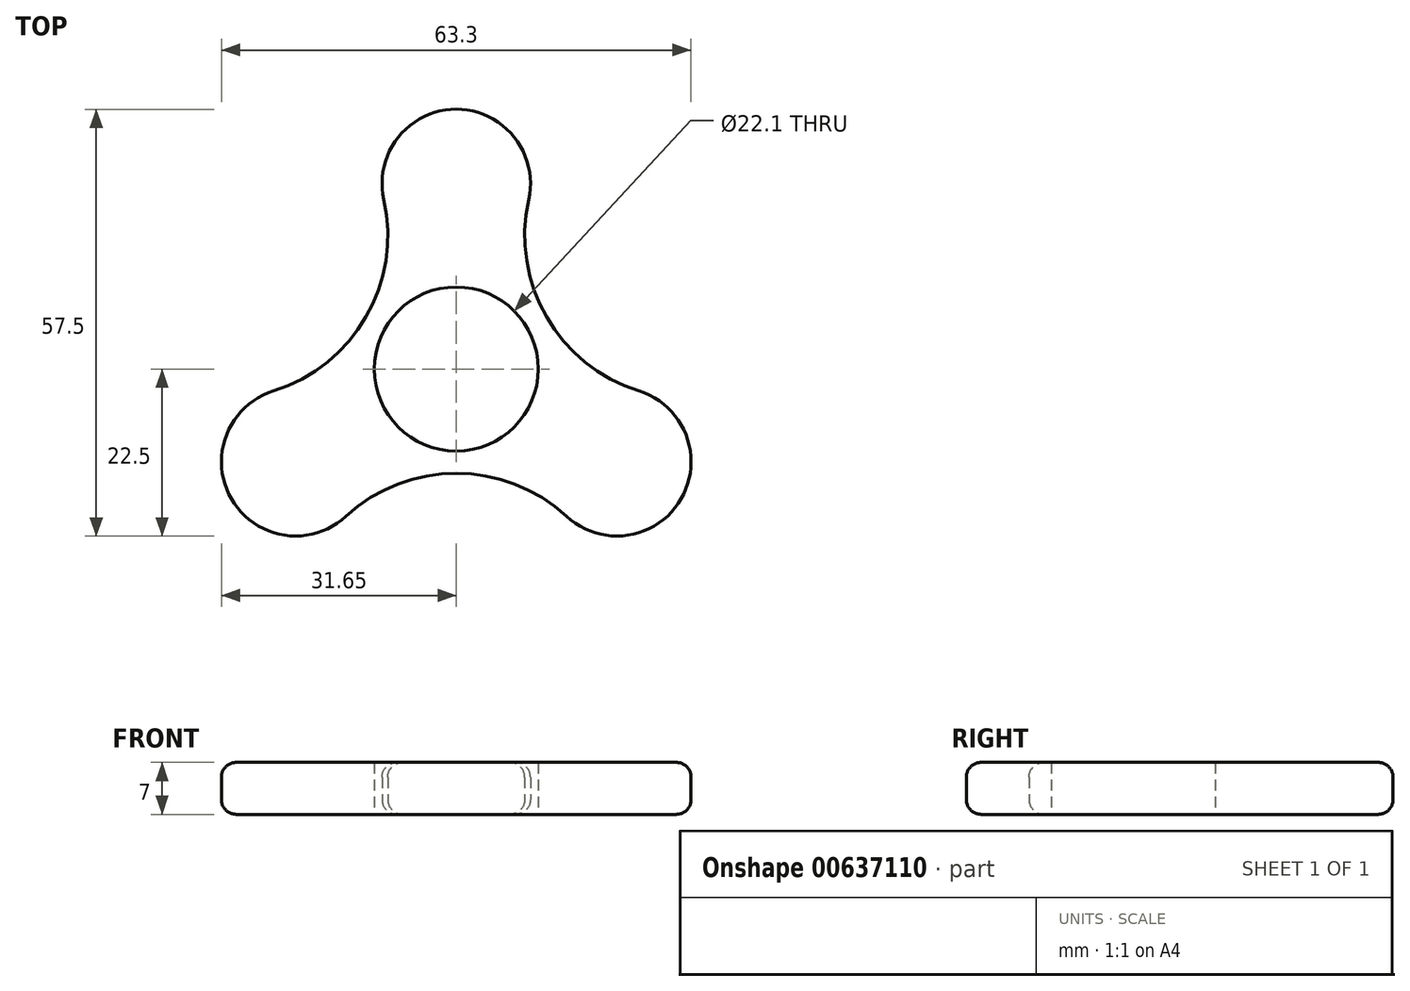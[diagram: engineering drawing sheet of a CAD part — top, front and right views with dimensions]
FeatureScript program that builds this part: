
annotation { "Feature Type Name" : "Feature", "Feature Type Description" : "" }
export const myFeature = defineFeature(function(context is Context, id is Id, definition is map)
    precondition{}
    {
        {
            var Q0;
            Q0=qCreatedBy(makeId("Top.planeOp"),FACE);
            var sketch = newSketch(context, id + "F0", { "sketchPlane" : qUnion([Q0])});
            skCircle(sketch, "E0", {"center": v(0, 0) * mm, "radius": 11.05 * mm});
            skLineSegment(sketch, "E1", {"start": v(0, 0) * mm, "end": v(0, 25) * mm});
            skLineSegment(sketch, "E2", {"start": v(0, 0) * mm, "end": v(-21.65, -12.5) * mm});
            skLineSegment(sketch, "E3", {"start": v(0, 0) * mm, "end": v(21.65, -12.5) * mm});
            skCircle(sketch, "E4", {"center": v(-21.65, -12.5) * mm, "radius": 10 * mm});
            skCircle(sketch, "E5", {"center": v(0, 25) * mm, "radius": 10 * mm});
            skCircle(sketch, "E6", {"center": v(21.65, -12.5) * mm, "radius": 10 * mm});
            skArc(sketch, "E7", {"start": v(-24.63, -2.96) * mm, "mid": v(-12.17, 7.03) * mm, "end": v(-9.76, 22.81) * mm});
            skArc(sketch, "E8", {"start": v(9.76, 22.81) * mm, "mid": v(12.17, 7.02) * mm, "end": v(24.63, -2.96) * mm});
            skArc(sketch, "E9", {"start": v(14.88, -19.86) * mm, "mid": v(0, -14.05) * mm, "end": v(-14.88, -19.86) * mm});
            skSolve(sketch);
        }
        {
            var Q0;
            {var subQ0=sQuery(id+"F0.wireOp",EDGE,"E4");var subQ1=makeQuery(id+"F0.imprint","INTERSECT",VERTEX,{"derivedFrom":[subQ0,sQuery(id+"F0.wireOp",EDGE,"E7")]});Q0=makeQuery(id+"F0.imprint","IMPRINT",FACE,{"disambiguationData":[TD([[makeQuery(id+"F0.imprint","IMPRINT",EDGE,{"disambiguationData":[TD([[subQ1,1.0]])],"derivedFrom":subQ0}),1.0]])]});}
            var Q1;
            {var subQ5=sQuery(id+"F0.wireOp",EDGE,"E7");Q1=makeQuery(id+"F0.imprint","IMPRINT",FACE,{"disambiguationData":[TD([[makeQuery(id+"F0.imprint","IMPRINT",EDGE,{"derivedFrom":subQ5}),-1.0]])]});}
            var Q2;
            {var subQ0=sQuery(id+"F0.wireOp",EDGE,"E8");Q2=makeQuery(id+"F0.imprint","IMPRINT",FACE,{"disambiguationData":[TD([[makeQuery(id+"F0.imprint","IMPRINT",EDGE,{"derivedFrom":subQ0}),-1.0]])]});}
            var Q3;
            {var subQ0=sQuery(id+"F0.wireOp",EDGE,"E5");var subQ1=makeQuery(id+"F0.imprint","INTERSECT",VERTEX,{"derivedFrom":[subQ0,sQuery(id+"F0.wireOp",EDGE,"E7")]});Q3=makeQuery(id+"F0.imprint","IMPRINT",FACE,{"disambiguationData":[TD([[makeQuery(id+"F0.imprint","IMPRINT",EDGE,{"disambiguationData":[TD([[subQ1,-1.0]])],"derivedFrom":subQ0}),1.0]])]});}
            var Q4;
            {var subQ0=sQuery(id+"F0.wireOp",EDGE,"E6");var subQ1=makeQuery(id+"F0.imprint","INTERSECT",VERTEX,{"derivedFrom":[subQ0,sQuery(id+"F0.wireOp",EDGE,"E8")]});Q4=makeQuery(id+"F0.imprint","IMPRINT",FACE,{"disambiguationData":[TD([[makeQuery(id+"F0.imprint","IMPRINT",EDGE,{"disambiguationData":[TD([[subQ1,-1.0]])],"derivedFrom":subQ0}),1.0]])]});}
            var Q5;
            {var subQ5=sQuery(id+"F0.wireOp",EDGE,"E9");Q5=makeQuery(id+"F0.imprint","IMPRINT",FACE,{"disambiguationData":[TD([[makeQuery(id+"F0.imprint","IMPRINT",EDGE,{"derivedFrom":subQ5}),-1.0]])]});}
            extrude(context, id + "F1", {"entities" : qUnion([Q0, Q1, Q2, Q3, Q4, Q5]), "depth" : 7 * mm, "offsetDistance" : 25 * mm});
        }
        {
            var Q0;
            Q0=makeQuery(id+"F1.opExtrude","CAP_EDGE",EDGE,{"disambiguationData":[OSD([sQuery(id+"F0.wireOp",EDGE,"E9")])],"isStart":false});
            var Q1;
            Q1=makeQuery(id+"F1.opExtrude","CAP_EDGE",EDGE,{"disambiguationData":[OSD([sQuery(id+"F0.wireOp",EDGE,"E9")])],"isStart":true});
            fillet(context, id + "F2", {"entities" : qUnion([Q0, Q1]), "radius" : 2 * mm, "tangentPropagation" : true, "allowEdgeOverflow" : false});
        }
    });
